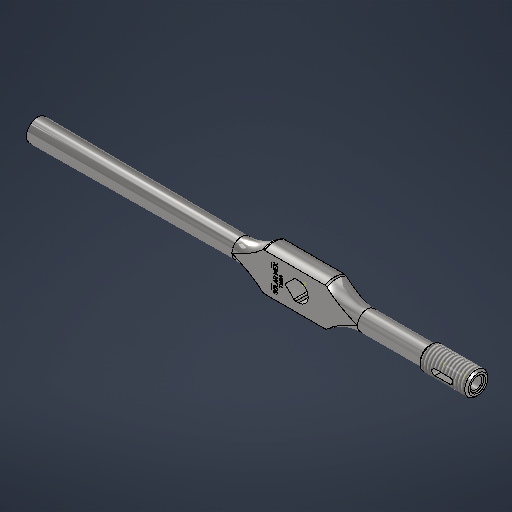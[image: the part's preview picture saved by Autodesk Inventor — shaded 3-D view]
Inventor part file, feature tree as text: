
AUTODESK INVENTOR PART (.ipt)
format: ipt  version: 2025.3 (Build 293356000, 356)  size: 475,648 bytes
history: native  units: mm
features: sketch x5, extrude x2, other x2, fillet x2, revolve x1, thread x1, plane x1, projected_geometry x1
ambient origin geometry x8: Origin, YZ Plane, XZ Plane, XY Plane, X Axis, Y Axis, Z Axis, Center Point
bodies: Solid1 (feature_tree)
feature tree (15):
  sketch  "Sketch1"  dims[d0=7.071068mm d3=2.071068mm]
  revolve  "Revolution1"  [1 undecoded]
  extrude  "Extrusion1"  Depth=65.0mm
  extrude  "Extrusion2"  Depth=1.5mm
  thread  "Thread1"  [1 undecoded]
  other  "Mark2"
  plane  "Work Plane1"
  fillet  "Fillet3"  Radius=6.0mm
  fillet  "Fillet4"  Radius=1.5mm
  sketch  "Sketch5"  dims[d24=1.0mm]
  other  "Work Axis1"
  sketch  "Sketch6"  dims[d25=12.0mm d26=1.0mm d27=1.0mm d28=90.0mm d29=25.0mm d32=360.0deg d33=3.05mm d34=8.0mm d35=0.0mm d36=0.0mm d37=10.0mm d38=0.0mm d39=0.0mm d40=10.0mm d41=11.5mm d42=140.0mm d43=23.0mm d44=0.0mm d46=8.0mm d47=1.0mm d48=50.0mm d49=2.0mm d50=10.0mm d52=10.0mm d54=123.748077mm d55=73.748077mm d56=1.5mm d57=32.503846mm d59=14.930565mm d60=4.048188mm d61=3.0mm d62=1.5mm d63=230.0mm d64=3.0mm]
  sketch  "Sketch2"  dims[d4=0.070967mm d6=65.0mm]
  sketch  "Sketch4"  dims[d7=10.0mm d8=22.0mm d11=6.0mm d17=6.0mm d20=1.5mm d21=1.0mm]
  projected_geometry  "Projected Loop1"
note: 2 required parameter values undecoded (feature->parameter linkage not recoverable at this tier; creation-order binding heuristic only, values carry confidence <= 0.55)